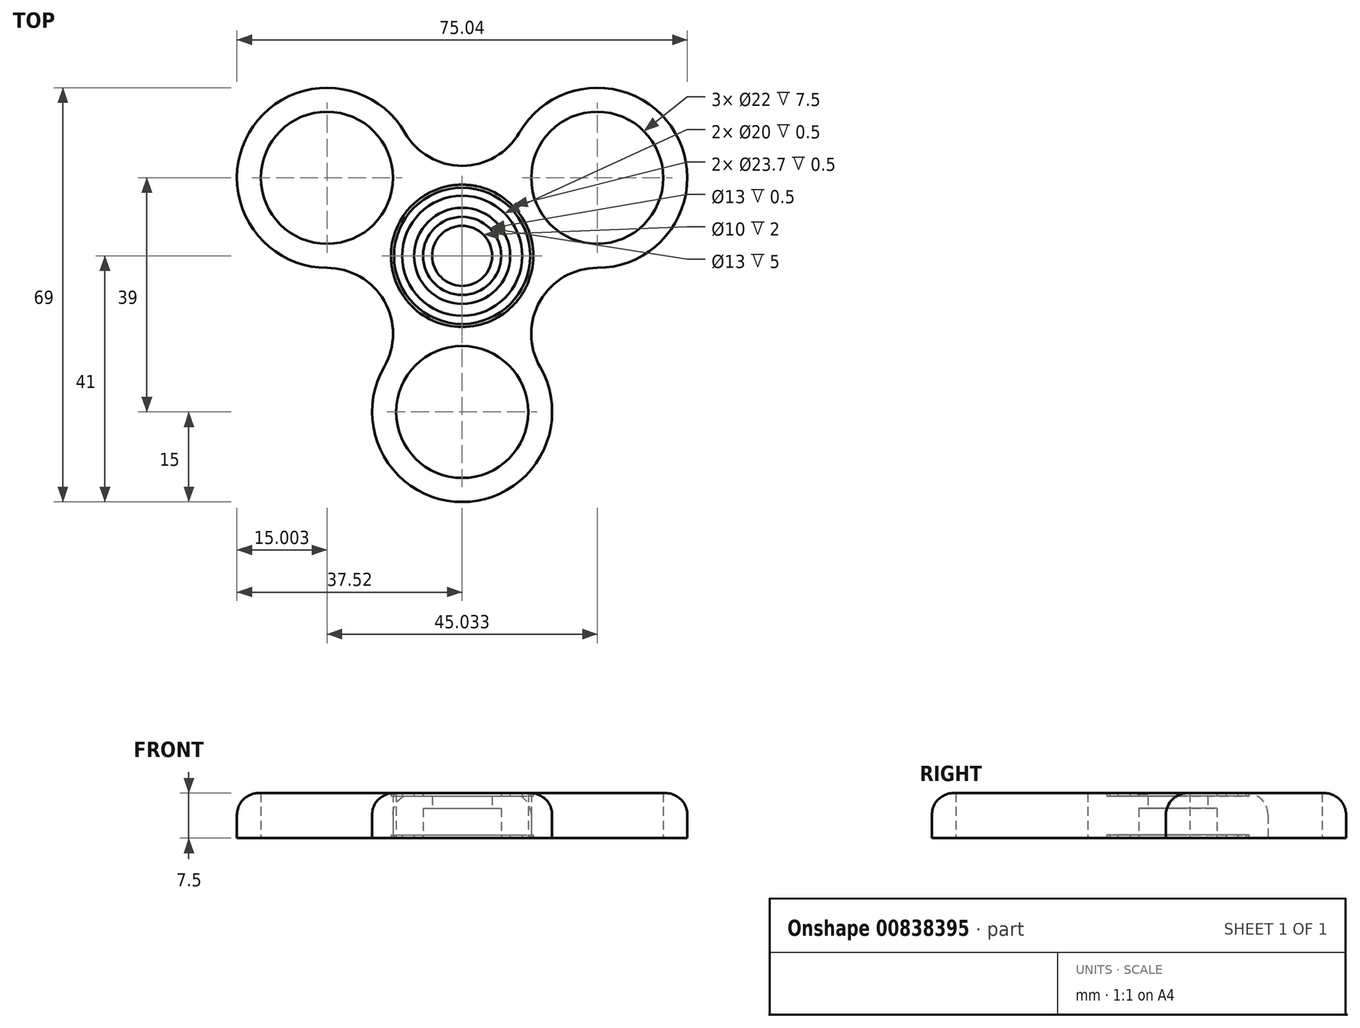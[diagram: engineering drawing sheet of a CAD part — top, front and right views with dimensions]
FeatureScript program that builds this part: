
annotation { "Feature Type Name" : "Feature", "Feature Type Description" : "" }
export const myFeature = defineFeature(function(context is Context, id is Id, definition is map)
    precondition{}
    {
        {
            var Q0;
            Q0=qCreatedBy(makeId("Front.planeOp"),FACE);
            var sketch = newSketch(context, id + "F0", { "sketchPlane" : qUnion([Q0])});
            skLineSegment(sketch, "E0", {"start": v(6.5, 5) * mm, "end": v(5, 5) * mm});
            skLineSegment(sketch, "E1", {"start": v(5, 5) * mm, "end": v(5, 7) * mm});
            skLineSegment(sketch, "E2", {"start": v(5, 7) * mm, "end": v(6.5, 7) * mm});
            skLineSegment(sketch, "E3", {"start": v(6.5, 7) * mm, "end": v(6.5, 7.5) * mm});
            skLineSegment(sketch, "E4", {"start": v(6.5, 7.5) * mm, "end": v(8, 7.5) * mm});
            skLineSegment(sketch, "E5", {"start": v(8, 7.5) * mm, "end": v(8, 7) * mm});
            skLineSegment(sketch, "E6", {"start": v(8, 7) * mm, "end": v(10, 7) * mm});
            skLineSegment(sketch, "E7", {"start": v(10, 7) * mm, "end": v(10, 7.5) * mm});
            skLineSegment(sketch, "E8", {"start": v(10, 7.5) * mm, "end": v(11.35, 7.5) * mm});
            skLineSegment(sketch, "E9", {"start": v(11.35, 7.5) * mm, "end": v(11.35, 7) * mm});
            skLineSegment(sketch, "E10", {"start": v(11.35, 7) * mm, "end": v(11.85, 7) * mm});
            skLineSegment(sketch, "E11", {"start": v(11.85, 7) * mm, "end": v(11.85, 7.5) * mm});
            skLineSegment(sketch, "E12", {"start": v(11.85, 7.5) * mm, "end": v(41, 7.5) * mm});
            skLineSegment(sketch, "E13", {"start": v(41, 7.5) * mm, "end": v(41, 0) * mm});
            skLineSegment(sketch, "E14", {"start": v(41, 0) * mm, "end": v(11.85, 0) * mm});
            skLineSegment(sketch, "E15", {"start": v(11.85, 0) * mm, "end": v(11.85, 0.5) * mm});
            skLineSegment(sketch, "E16", {"start": v(11.85, 0.5) * mm, "end": v(11.35, 0.5) * mm});
            skLineSegment(sketch, "E17", {"start": v(11.35, 0.5) * mm, "end": v(11.35, 0) * mm});
            skLineSegment(sketch, "E18", {"start": v(10, 0) * mm, "end": v(10, 0.5) * mm});
            skLineSegment(sketch, "E19", {"start": v(10, 0.5) * mm, "end": v(8, 0.5) * mm});
            skLineSegment(sketch, "E20", {"start": v(8, 0.5) * mm, "end": v(8, 0) * mm});
            skLineSegment(sketch, "E21", {"start": v(8, 0) * mm, "end": v(6.5, 0) * mm});
            skLineSegment(sketch, "E22", {"start": v(6.5, 0) * mm, "end": v(6.5, 5) * mm});
            skLineSegment(sketch, "E23", {"start": v(10, 0) * mm, "end": v(11.35, 0) * mm});
            skLineSegment(sketch, "E24", {"start": v(0, -9.17) * mm, "end": v(0, 20.6) * mm, "construction": true});
            skSolve(sketch);
        }
        {
            var Q0;
            Q0=makeQuery(id+"F0.imprint","IMPRINT",FACE,{"disambiguationData":[TD([[makeQuery(id+"F0.imprint","IMPRINT",EDGE,{"derivedFrom":sQuery(id+"F0.wireOp",EDGE,"E0")}),-1.0]])]});
            var Q1;
            Q1=sQuery(id+"F0.wireOp",EDGE,"E24");
            revolve(context, id + "F1", {"surfaceOperationType" : NewSurfaceOperationType.NEW, "entities" : qUnion([Q0]), "axis" : qUnion([Q1]), "revolveType" : RevolveType.FULL});
        }
        {
            var Q0;
            Q0=makeQuery(id+"F1.opRevolve","SWEPT_FACE",FACE,{"disambiguationData":[OSD([sQuery(id+"F0.wireOp",EDGE,"E14")])]});
            var sketch = newSketch(context, id + "F2", { "sketchPlane" : qUnion([Q0])});
            skCircle(sketch, "E25", {"center": v(0, -26) * mm, "radius": 11 * mm});
            skCircle(sketch, "E26", {"center": v(0, -26) * mm, "radius": 15 * mm});
            skCircle(sketch, "E27.1.0", {"center": v(22.52, -13) * mm, "radius": 11 * mm});
            skCircle(sketch, "E27.1.1", {"center": v(22.52, -13) * mm, "radius": 15 * mm});
            skCircle(sketch, "E27.2.0", {"center": v(22.52, 13) * mm, "radius": 11 * mm});
            skCircle(sketch, "E27.2.1", {"center": v(22.52, 13) * mm, "radius": 15 * mm});
            skCircle(sketch, "E27.3.0", {"center": v(0, 26) * mm, "radius": 11 * mm});
            skCircle(sketch, "E27.3.1", {"center": v(0, 26) * mm, "radius": 15 * mm});
            skCircle(sketch, "E27.4.0", {"center": v(-22.52, 13) * mm, "radius": 11 * mm});
            skCircle(sketch, "E27.4.1", {"center": v(-22.52, 13) * mm, "radius": 15 * mm});
            skCircle(sketch, "E27.5.0", {"center": v(-22.52, -13) * mm, "radius": 11 * mm});
            skCircle(sketch, "E27.5.1", {"center": v(-22.52, -13) * mm, "radius": 15 * mm});
            skPoint(sketch, "E27.center", {"position": v(0, 0) * mm});
            skSolve(sketch);
        }
        {
            var Q0;
            {var subQ0=sQuery(id+"F2.wireOp",EDGE,"E27.4.0");var subQ1=makeQuery(id+"F2.imprint","INTERSECT",VERTEX,{"derivedFrom":[sQuery(id+"F2.wireOp",EDGE,"E27.3.1"),subQ0]});Q0=makeQuery(id+"F2.imprint","IMPRINT",FACE,{"disambiguationData":[TD([[makeQuery(id+"F2.imprint","IMPRINT",EDGE,{"disambiguationData":[TD([[subQ1,1.0]])],"derivedFrom":subQ0}),1.0]])]});}
            var Q1;
            {var subQ4=sQuery(id+"F2.wireOp",EDGE,"E27.3.1");var subQ6=sQuery(id+"F2.wireOp",EDGE,"E27.4.0");var subQ7=makeQuery(id+"F2.imprint","INTERSECT",VERTEX,{"derivedFrom":[subQ4,subQ6]});Q1=makeQuery(id+"F2.imprint","IMPRINT",FACE,{"disambiguationData":[TD([[makeQuery(id+"F2.imprint","IMPRINT",EDGE,{"disambiguationData":[TD([[subQ7,1.0]])],"derivedFrom":subQ4}),-1.0]])]});}
            var Q2;
            {var subQ0=sQuery(id+"F2.wireOp",EDGE,"E27.4.1");var subQ1=sQuery(id+"F2.wireOp",EDGE,"E27.3.1");var subQ2=makeQuery(id+"F2.imprint","INTERSECT",VERTEX,{"disambiguationData":[OD(0.0)],"derivedFrom":[subQ1,subQ0]});Q2=makeQuery(id+"F2.imprint","IMPRINT",FACE,{"disambiguationData":[TD([[makeQuery(id+"F2.imprint","IMPRINT",EDGE,{"disambiguationData":[TD([[subQ2,1.0]])],"derivedFrom":subQ1}),-1.0]])]});}
            var Q3;
            {var subQ0=sQuery(id+"F2.wireOp",EDGE,"E27.3.1");var subQ1=sQuery(id+"F2.wireOp",EDGE,"E27.2.1");var subQ2=makeQuery(id+"F2.imprint","INTERSECT",VERTEX,{"disambiguationData":[OD(0.0)],"derivedFrom":[subQ1,subQ0]});Q3=makeQuery(id+"F2.imprint","IMPRINT",FACE,{"disambiguationData":[TD([[makeQuery(id+"F2.imprint","IMPRINT",EDGE,{"disambiguationData":[TD([[subQ2,1.0]])],"derivedFrom":subQ1}),-1.0]])]});}
            var Q4;
            {var subQ0=sQuery(id+"F2.wireOp",EDGE,"E27.2.1");var subQ1=sQuery(id+"F2.wireOp",EDGE,"E27.1.1");var subQ2=makeQuery(id+"F2.imprint","INTERSECT",VERTEX,{"disambiguationData":[OD(0.0)],"derivedFrom":[subQ1,subQ0]});Q4=makeQuery(id+"F2.imprint","IMPRINT",FACE,{"disambiguationData":[TD([[makeQuery(id+"F2.imprint","IMPRINT",EDGE,{"disambiguationData":[TD([[subQ2,1.0]])],"derivedFrom":subQ1}),-1.0]])]});}
            var Q5;
            {var subQ0=sQuery(id+"F2.wireOp",EDGE,"E27.1.1");var subQ1=sQuery(id+"F2.wireOp",EDGE,"E26");var subQ2=makeQuery(id+"F2.imprint","INTERSECT",VERTEX,{"disambiguationData":[OD(0.0)],"derivedFrom":[subQ1,subQ0]});Q5=makeQuery(id+"F2.imprint","IMPRINT",FACE,{"disambiguationData":[TD([[makeQuery(id+"F2.imprint","IMPRINT",EDGE,{"disambiguationData":[TD([[subQ2,1.0]])],"derivedFrom":subQ1}),-1.0]])]});}
            var Q6;
            {var subQ0=sQuery(id+"F2.wireOp",EDGE,"E27.5.1");var subQ1=sQuery(id+"F2.wireOp",EDGE,"E27.4.1");var subQ2=makeQuery(id+"F2.imprint","INTERSECT",VERTEX,{"disambiguationData":[OD(0.0)],"derivedFrom":[subQ1,subQ0]});Q6=makeQuery(id+"F2.imprint","IMPRINT",FACE,{"disambiguationData":[TD([[makeQuery(id+"F2.imprint","IMPRINT",EDGE,{"disambiguationData":[TD([[subQ2,1.0]])],"derivedFrom":subQ1}),-1.0]])]});}
            var Q7;
            {var subQ0=sQuery(id+"F2.wireOp",EDGE,"E27.5.1");var subQ1=sQuery(id+"F2.wireOp",EDGE,"E26");var subQ2=makeQuery(id+"F2.imprint","INTERSECT",VERTEX,{"disambiguationData":[OD(1.0)],"derivedFrom":[subQ1,subQ0]});Q7=makeQuery(id+"F2.imprint","IMPRINT",FACE,{"disambiguationData":[TD([[makeQuery(id+"F2.imprint","IMPRINT",EDGE,{"disambiguationData":[TD([[subQ2,-1.0]])],"derivedFrom":subQ1}),-1.0]])]});}
            var Q8;
            {var subQ0=sQuery(id+"F2.wireOp",EDGE,"E27.2.0");var subQ1=makeQuery(id+"F2.imprint","INTERSECT",VERTEX,{"derivedFrom":[sQuery(id+"F2.wireOp",EDGE,"E27.1.1"),subQ0]});Q8=makeQuery(id+"F2.imprint","IMPRINT",FACE,{"disambiguationData":[TD([[makeQuery(id+"F2.imprint","IMPRINT",EDGE,{"disambiguationData":[TD([[subQ1,1.0]])],"derivedFrom":subQ0}),1.0]])]});}
            var Q9;
            {var subQ4=sQuery(id+"F2.wireOp",EDGE,"E27.1.1");var subQ6=sQuery(id+"F2.wireOp",EDGE,"E27.2.0");var subQ7=makeQuery(id+"F2.imprint","INTERSECT",VERTEX,{"derivedFrom":[subQ4,subQ6]});Q9=makeQuery(id+"F2.imprint","IMPRINT",FACE,{"disambiguationData":[TD([[makeQuery(id+"F2.imprint","IMPRINT",EDGE,{"disambiguationData":[TD([[subQ7,1.0]])],"derivedFrom":subQ4}),-1.0]])]});}
            var Q10;
            {var subQ0=sQuery(id+"F2.wireOp",EDGE,"E25");var subQ1=makeQuery(id+"F2.imprint","INTERSECT",VERTEX,{"derivedFrom":[subQ0,sQuery(id+"F2.wireOp",EDGE,"E27.1.1")]});Q10=makeQuery(id+"F2.imprint","IMPRINT",FACE,{"disambiguationData":[TD([[makeQuery(id+"F2.imprint","IMPRINT",EDGE,{"disambiguationData":[TD([[subQ1,-1.0]])],"derivedFrom":subQ0}),1.0]])]});}
            var Q11;
            {var subQ0=sQuery(id+"F2.wireOp",EDGE,"E27.1.1");var subQ4=sQuery(id+"F2.wireOp",EDGE,"E25");var subQ5=makeQuery(id+"F2.imprint","INTERSECT",VERTEX,{"derivedFrom":[subQ4,subQ0]});Q11=makeQuery(id+"F2.imprint","IMPRINT",FACE,{"disambiguationData":[TD([[makeQuery(id+"F2.imprint","IMPRINT",EDGE,{"disambiguationData":[TD([[subQ5,1.0]])],"derivedFrom":subQ4}),-1.0]])]});}
            var Q12;
            {var subQ0=sQuery(id+"F2.wireOp",EDGE,"E27.5.0");var subQ1=makeQuery(id+"F2.imprint","INTERSECT",VERTEX,{"derivedFrom":[sQuery(id+"F2.wireOp",EDGE,"E26"),subQ0]});Q12=makeQuery(id+"F2.imprint","IMPRINT",FACE,{"disambiguationData":[TD([[makeQuery(id+"F2.imprint","IMPRINT",EDGE,{"disambiguationData":[TD([[subQ1,-1.0]])],"derivedFrom":subQ0}),1.0]])]});}
            var Q13;
            {var subQ0=sQuery(id+"F2.wireOp",EDGE,"E27.3.0");var subQ1=makeQuery(id+"F2.imprint","INTERSECT",VERTEX,{"derivedFrom":[sQuery(id+"F2.wireOp",EDGE,"E27.2.1"),subQ0]});Q13=makeQuery(id+"F2.imprint","IMPRINT",FACE,{"disambiguationData":[TD([[makeQuery(id+"F2.imprint","IMPRINT",EDGE,{"disambiguationData":[TD([[subQ1,1.0]])],"derivedFrom":subQ0}),1.0]])]});}
            var Q14;
            {var subQ0=sQuery(id+"F2.wireOp",EDGE,"E27.1.0");var subQ1=makeQuery(id+"F2.imprint","INTERSECT",VERTEX,{"derivedFrom":[sQuery(id+"F2.wireOp",EDGE,"E26"),subQ0]});Q14=makeQuery(id+"F2.imprint","IMPRINT",FACE,{"disambiguationData":[TD([[makeQuery(id+"F2.imprint","IMPRINT",EDGE,{"disambiguationData":[TD([[subQ1,1.0]])],"derivedFrom":subQ0}),1.0]])]});}
            extrude(context, id + "F3", {"entities" : qUnion([Q0, Q1, Q2, Q3, Q4, Q5, Q6, Q7, Q8, Q9, Q10, Q11, Q12, Q13, Q14]), "operationType" : NewBodyOperationType.REMOVE, "endBound" : BoundingType.THROUGH_ALL, "oppositeDirection" : true, "depth" : 25 * mm, "offsetDistance" : 25 * mm});
        }
        {
            var Q0;
            {var subQ0=sQuery(id+"F2.wireOp",EDGE,"E27.5.1");var subQ1=makeQuery(id+"F2.imprint","INTERSECT",VERTEX,{"disambiguationData":[OD(0.0)],"derivedFrom":[sQuery(id+"F2.wireOp",EDGE,"E27.4.1"),subQ0]});var subQ3=makeQuery(id+"F2.imprint","INTERSECT",VERTEX,{"disambiguationData":[OD(1.0)],"derivedFrom":[sQuery(id+"F2.wireOp",EDGE,"E26"),subQ0]});Q0=makeQuery(id+"F3.boolean.opBoolean","TWEAK_EDGE",EDGE,{"derivedFrom":[makeQuery(id+"F3.opExtrude","CAP_EDGE",EDGE,{"disambiguationData":[OSD([subQ0]),TDD([makeQuery(id+"F2.imprint","IMPRINT",EDGE,{"disambiguationData":[TD([[makeQuery(id+"F2.imprint","INTERSECT",VERTEX,{"derivedFrom":[sQuery(id+"F2.wireOp",EDGE,"E25"),subQ0]}),1.0]])],"derivedFrom":subQ0}),makeQuery(id+"F2.imprint","IMPRINT",EDGE,{"disambiguationData":[TD([[subQ3,1.0]])],"derivedFrom":subQ0})])],"isStart":true}),makeQuery(id+"F3.opExtrude","CAP_EDGE",EDGE,{"disambiguationData":[OSD([subQ0]),TDD([makeQuery(id+"F2.imprint","IMPRINT",EDGE,{"disambiguationData":[TD([[makeQuery(id+"F2.imprint","INTERSECT",VERTEX,{"derivedFrom":[sQuery(id+"F2.wireOp",EDGE,"E27.4.0"),subQ0]}),-1.0]])],"derivedFrom":subQ0}),makeQuery(id+"F2.imprint","IMPRINT",EDGE,{"disambiguationData":[TD([[subQ1,-1.0]])],"derivedFrom":subQ0})])],"isStart":true})]});}
            var Q1;
            Q1=makeQuery(id+"F3.boolean.opBoolean","COPY",EDGE,{"derivedFrom":makeQuery(id+"F3.opExtrude","CAP_EDGE",EDGE,{"disambiguationData":[OSD([sQuery(id+"F2.wireOp",EDGE,"E25")])],"isStart":true})});
            var Q2;
            Q2=makeQuery(id+"F3.boolean.opBoolean","COPY",EDGE,{"derivedFrom":makeQuery(id+"F3.opExtrude","CAP_EDGE",EDGE,{"disambiguationData":[OSD([sQuery(id+"F2.wireOp",EDGE,"E27.4.0")])],"isStart":true})});
            var Q3;
            {var subQ0=sQuery(id+"F2.wireOp",EDGE,"E27.3.1");var subQ1=makeQuery(id+"F2.imprint","INTERSECT",VERTEX,{"disambiguationData":[OD(0.0)],"derivedFrom":[sQuery(id+"F2.wireOp",EDGE,"E27.2.1"),subQ0]});var subQ3=makeQuery(id+"F2.imprint","INTERSECT",VERTEX,{"disambiguationData":[OD(0.0)],"derivedFrom":[subQ0,sQuery(id+"F2.wireOp",EDGE,"E27.4.1")]});Q3=makeQuery(id+"F3.boolean.opBoolean","TWEAK_EDGE",EDGE,{"derivedFrom":[makeQuery(id+"F3.opExtrude","CAP_EDGE",EDGE,{"disambiguationData":[OSD([subQ0]),TDD([makeQuery(id+"F2.imprint","IMPRINT",EDGE,{"disambiguationData":[TD([[makeQuery(id+"F2.imprint","INTERSECT",VERTEX,{"derivedFrom":[subQ0,sQuery(id+"F2.wireOp",EDGE,"E27.4.0")]}),1.0]])],"derivedFrom":subQ0}),makeQuery(id+"F2.imprint","IMPRINT",EDGE,{"disambiguationData":[TD([[subQ3,1.0]])],"derivedFrom":subQ0})])],"isStart":true}),makeQuery(id+"F3.opExtrude","CAP_EDGE",EDGE,{"disambiguationData":[OSD([subQ0]),TDD([makeQuery(id+"F2.imprint","IMPRINT",EDGE,{"disambiguationData":[TD([[makeQuery(id+"F2.imprint","INTERSECT",VERTEX,{"derivedFrom":[sQuery(id+"F2.wireOp",EDGE,"E27.2.0"),subQ0]}),-1.0]])],"derivedFrom":subQ0}),makeQuery(id+"F2.imprint","IMPRINT",EDGE,{"disambiguationData":[TD([[subQ1,-1.0]])],"derivedFrom":subQ0})])],"isStart":true})]});}
            var Q4;
            Q4=makeQuery(id+"F3.boolean.opBoolean","COPY",EDGE,{"derivedFrom":makeQuery(id+"F3.opExtrude","CAP_EDGE",EDGE,{"disambiguationData":[OSD([sQuery(id+"F2.wireOp",EDGE,"E27.2.0")])],"isStart":true})});
            var Q5;
            {var subQ0=sQuery(id+"F2.wireOp",EDGE,"E27.1.1");var subQ1=makeQuery(id+"F2.imprint","INTERSECT",VERTEX,{"disambiguationData":[OD(0.0)],"derivedFrom":[sQuery(id+"F2.wireOp",EDGE,"E26"),subQ0]});var subQ3=makeQuery(id+"F2.imprint","INTERSECT",VERTEX,{"disambiguationData":[OD(0.0)],"derivedFrom":[subQ0,sQuery(id+"F2.wireOp",EDGE,"E27.2.1")]});Q5=makeQuery(id+"F3.boolean.opBoolean","TWEAK_EDGE",EDGE,{"derivedFrom":[makeQuery(id+"F3.opExtrude","CAP_EDGE",EDGE,{"disambiguationData":[OSD([subQ0]),TDD([makeQuery(id+"F2.imprint","IMPRINT",EDGE,{"disambiguationData":[TD([[makeQuery(id+"F2.imprint","INTERSECT",VERTEX,{"derivedFrom":[subQ0,sQuery(id+"F2.wireOp",EDGE,"E27.2.0")]}),1.0]])],"derivedFrom":subQ0}),makeQuery(id+"F2.imprint","IMPRINT",EDGE,{"disambiguationData":[TD([[subQ3,1.0]])],"derivedFrom":subQ0})])],"isStart":true}),makeQuery(id+"F3.opExtrude","CAP_EDGE",EDGE,{"disambiguationData":[OSD([subQ0]),TDD([makeQuery(id+"F2.imprint","IMPRINT",EDGE,{"disambiguationData":[TD([[makeQuery(id+"F2.imprint","INTERSECT",VERTEX,{"derivedFrom":[sQuery(id+"F2.wireOp",EDGE,"E25"),subQ0]}),-1.0]])],"derivedFrom":subQ0}),makeQuery(id+"F2.imprint","IMPRINT",EDGE,{"disambiguationData":[TD([[subQ1,-1.0]])],"derivedFrom":subQ0})])],"isStart":true})]});}
            var Q6;
            {var subQ0=sQuery(id+"F2.wireOp",EDGE,"E27.5.1");var subQ1=makeQuery(id+"F2.imprint","INTERSECT",VERTEX,{"disambiguationData":[OD(0.0)],"derivedFrom":[sQuery(id+"F2.wireOp",EDGE,"E27.4.1"),subQ0]});var subQ3=makeQuery(id+"F2.imprint","INTERSECT",VERTEX,{"disambiguationData":[OD(1.0)],"derivedFrom":[sQuery(id+"F2.wireOp",EDGE,"E26"),subQ0]});Q6=makeQuery(id+"F3.boolean.opBoolean","INTERSECT",EDGE,{"derivedFrom":[makeQuery(id+"F1.opRevolve","SWEPT_FACE",FACE,{"disambiguationData":[OSD([sQuery(id+"F0.wireOp",EDGE,"E12")])]}),makeQuery(id+"F3.opExtrude","SWEPT_FACE",FACE,{"disambiguationData":[OSD([subQ0]),TDD([makeQuery(id+"F2.imprint","IMPRINT",EDGE,{"disambiguationData":[TD([[makeQuery(id+"F2.imprint","INTERSECT",VERTEX,{"derivedFrom":[sQuery(id+"F2.wireOp",EDGE,"E25"),subQ0]}),1.0]])],"derivedFrom":subQ0}),makeQuery(id+"F2.imprint","IMPRINT",EDGE,{"disambiguationData":[TD([[subQ3,1.0]])],"derivedFrom":subQ0})])]}),makeQuery(id+"F3.opExtrude","SWEPT_FACE",FACE,{"disambiguationData":[OSD([subQ0]),TDD([makeQuery(id+"F2.imprint","IMPRINT",EDGE,{"disambiguationData":[TD([[makeQuery(id+"F2.imprint","INTERSECT",VERTEX,{"derivedFrom":[sQuery(id+"F2.wireOp",EDGE,"E27.4.0"),subQ0]}),-1.0]])],"derivedFrom":subQ0}),makeQuery(id+"F2.imprint","IMPRINT",EDGE,{"disambiguationData":[TD([[subQ1,-1.0]])],"derivedFrom":subQ0})])]})]});}
            var Q7;
            Q7=makeQuery(id+"F3.boolean.opBoolean","INTERSECT",EDGE,{"derivedFrom":[makeQuery(id+"F1.opRevolve","SWEPT_FACE",FACE,{"disambiguationData":[OSD([sQuery(id+"F0.wireOp",EDGE,"E12")])]}),makeQuery(id+"F3.opExtrude","SWEPT_FACE",FACE,{"disambiguationData":[OSD([sQuery(id+"F2.wireOp",EDGE,"E25")])]})]});
            var Q8;
            {var subQ0=sQuery(id+"F2.wireOp",EDGE,"E27.1.1");var subQ1=makeQuery(id+"F2.imprint","INTERSECT",VERTEX,{"disambiguationData":[OD(0.0)],"derivedFrom":[sQuery(id+"F2.wireOp",EDGE,"E26"),subQ0]});var subQ3=makeQuery(id+"F2.imprint","INTERSECT",VERTEX,{"disambiguationData":[OD(0.0)],"derivedFrom":[subQ0,sQuery(id+"F2.wireOp",EDGE,"E27.2.1")]});Q8=makeQuery(id+"F3.boolean.opBoolean","INTERSECT",EDGE,{"derivedFrom":[makeQuery(id+"F1.opRevolve","SWEPT_FACE",FACE,{"disambiguationData":[OSD([sQuery(id+"F0.wireOp",EDGE,"E12")])]}),makeQuery(id+"F3.opExtrude","SWEPT_FACE",FACE,{"disambiguationData":[OSD([subQ0]),TDD([makeQuery(id+"F2.imprint","IMPRINT",EDGE,{"disambiguationData":[TD([[makeQuery(id+"F2.imprint","INTERSECT",VERTEX,{"derivedFrom":[subQ0,sQuery(id+"F2.wireOp",EDGE,"E27.2.0")]}),1.0]])],"derivedFrom":subQ0}),makeQuery(id+"F2.imprint","IMPRINT",EDGE,{"disambiguationData":[TD([[subQ3,1.0]])],"derivedFrom":subQ0})])]}),makeQuery(id+"F3.opExtrude","SWEPT_FACE",FACE,{"disambiguationData":[OSD([subQ0]),TDD([makeQuery(id+"F2.imprint","IMPRINT",EDGE,{"disambiguationData":[TD([[makeQuery(id+"F2.imprint","INTERSECT",VERTEX,{"derivedFrom":[sQuery(id+"F2.wireOp",EDGE,"E25"),subQ0]}),-1.0]])],"derivedFrom":subQ0}),makeQuery(id+"F2.imprint","IMPRINT",EDGE,{"disambiguationData":[TD([[subQ1,-1.0]])],"derivedFrom":subQ0})])]})]});}
            var Q9;
            Q9=makeQuery(id+"F3.boolean.opBoolean","INTERSECT",EDGE,{"derivedFrom":[makeQuery(id+"F1.opRevolve","SWEPT_FACE",FACE,{"disambiguationData":[OSD([sQuery(id+"F0.wireOp",EDGE,"E12")])]}),makeQuery(id+"F3.opExtrude","SWEPT_FACE",FACE,{"disambiguationData":[OSD([sQuery(id+"F2.wireOp",EDGE,"E27.4.0")])]})]});
            var Q10;
            {var subQ0=sQuery(id+"F2.wireOp",EDGE,"E27.3.1");var subQ1=makeQuery(id+"F2.imprint","INTERSECT",VERTEX,{"disambiguationData":[OD(0.0)],"derivedFrom":[sQuery(id+"F2.wireOp",EDGE,"E27.2.1"),subQ0]});var subQ3=makeQuery(id+"F2.imprint","INTERSECT",VERTEX,{"disambiguationData":[OD(0.0)],"derivedFrom":[subQ0,sQuery(id+"F2.wireOp",EDGE,"E27.4.1")]});Q10=makeQuery(id+"F3.boolean.opBoolean","INTERSECT",EDGE,{"derivedFrom":[makeQuery(id+"F1.opRevolve","SWEPT_FACE",FACE,{"disambiguationData":[OSD([sQuery(id+"F0.wireOp",EDGE,"E12")])]}),makeQuery(id+"F3.opExtrude","SWEPT_FACE",FACE,{"disambiguationData":[OSD([subQ0]),TDD([makeQuery(id+"F2.imprint","IMPRINT",EDGE,{"disambiguationData":[TD([[makeQuery(id+"F2.imprint","INTERSECT",VERTEX,{"derivedFrom":[subQ0,sQuery(id+"F2.wireOp",EDGE,"E27.4.0")]}),1.0]])],"derivedFrom":subQ0}),makeQuery(id+"F2.imprint","IMPRINT",EDGE,{"disambiguationData":[TD([[subQ3,1.0]])],"derivedFrom":subQ0})])]}),makeQuery(id+"F3.opExtrude","SWEPT_FACE",FACE,{"disambiguationData":[OSD([subQ0]),TDD([makeQuery(id+"F2.imprint","IMPRINT",EDGE,{"disambiguationData":[TD([[makeQuery(id+"F2.imprint","INTERSECT",VERTEX,{"derivedFrom":[sQuery(id+"F2.wireOp",EDGE,"E27.2.0"),subQ0]}),-1.0]])],"derivedFrom":subQ0}),makeQuery(id+"F2.imprint","IMPRINT",EDGE,{"disambiguationData":[TD([[subQ1,-1.0]])],"derivedFrom":subQ0})])]})]});}
            var Q11;
            Q11=makeQuery(id+"F3.boolean.opBoolean","INTERSECT",EDGE,{"derivedFrom":[makeQuery(id+"F1.opRevolve","SWEPT_FACE",FACE,{"disambiguationData":[OSD([sQuery(id+"F0.wireOp",EDGE,"E12")])]}),makeQuery(id+"F3.opExtrude","SWEPT_FACE",FACE,{"disambiguationData":[OSD([sQuery(id+"F2.wireOp",EDGE,"E27.2.0")])]})]});
            fillet(context, id + "F4", {"entities" : qUnion([Q0, Q1, Q2, Q3, Q4, Q5, Q6, Q7, Q8, Q9, Q10, Q11]), "radius" : 3.6 * mm, "tangentPropagation" : true, "allowEdgeOverflow" : false});
        }
    });
